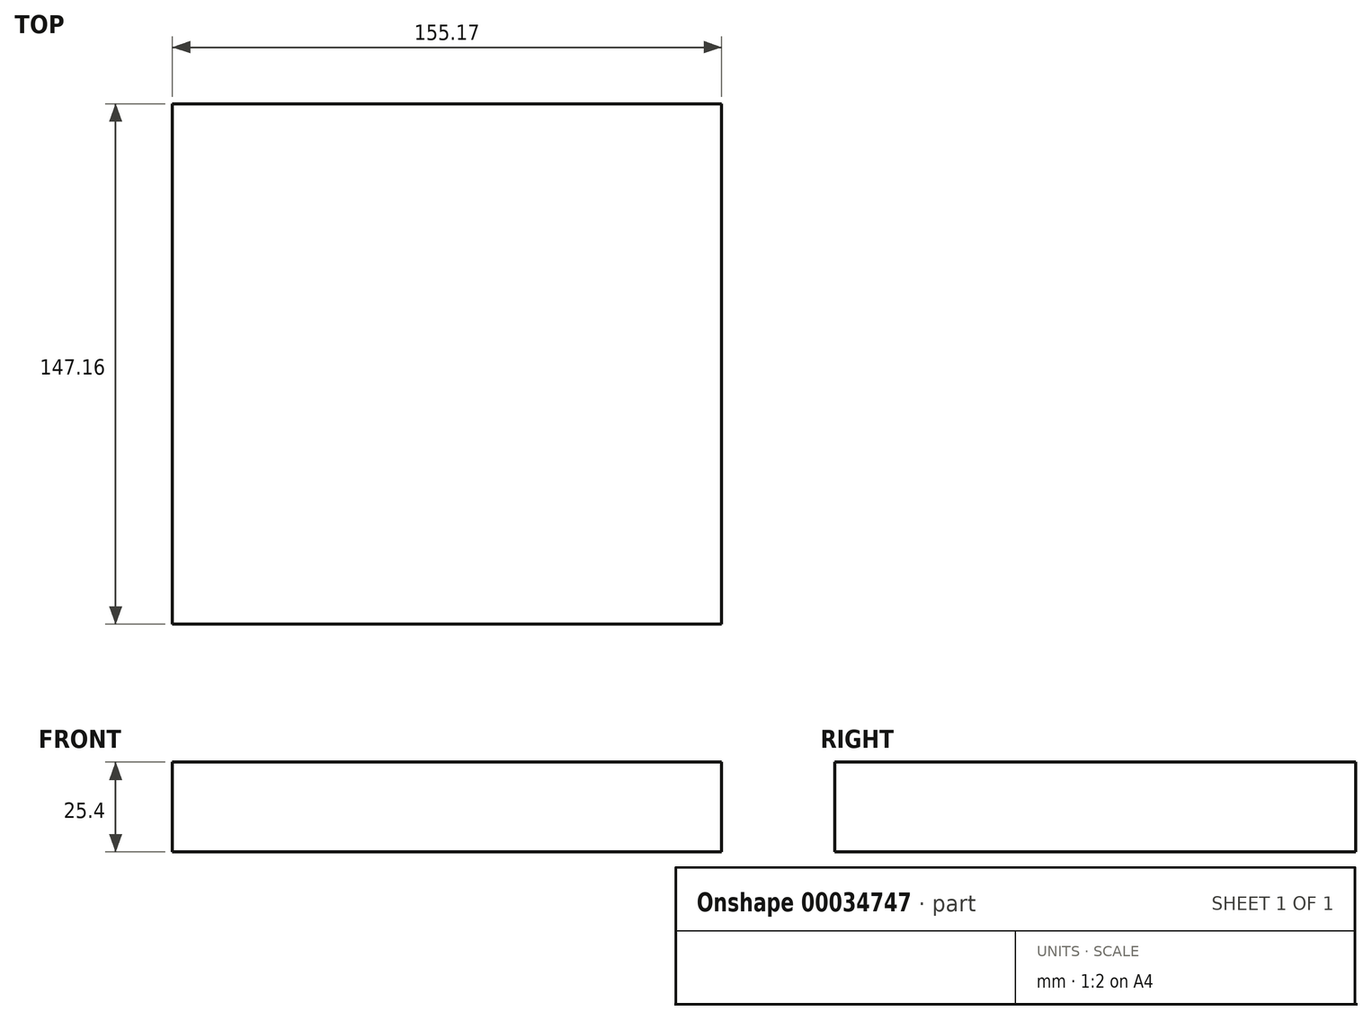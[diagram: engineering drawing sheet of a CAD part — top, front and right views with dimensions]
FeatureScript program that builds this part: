
annotation { "Feature Type Name" : "Feature", "Feature Type Description" : "" }
export const myFeature = defineFeature(function(context is Context, id is Id, definition is map)
    precondition{}
    {
        {
            var Q0;
            Q0=qCreatedBy(makeId("Top.planeOp"),FACE);
            var sketch = newSketch(context, id + "F0", { "sketchPlane" : qUnion([Q0])});
            skLineSegment(sketch, "E0.bottom", {"start": v(-76.18, 71.48) * mm, "end": v(79, 71.48) * mm});
            skLineSegment(sketch, "E0.top", {"start": v(-76.18, -75.68) * mm, "end": v(79, -75.68) * mm});
            skLineSegment(sketch, "E0.left", {"start": v(-76.18, 71.48) * mm, "end": v(-76.18, -75.68) * mm});
            skLineSegment(sketch, "E0.right", {"start": v(79, 71.48) * mm, "end": v(79, -75.68) * mm});
            skLineSegment(sketch, "E1.bottom", {"start": v(210.44, -47.96) * mm, "end": v(212.67, -47.96) * mm});
            skLineSegment(sketch, "E1.top", {"start": v(210.44, 119.08) * mm, "end": v(212.67, 119.08) * mm});
            skLineSegment(sketch, "E1.left", {"start": v(210.44, -47.96) * mm, "end": v(210.44, 119.08) * mm});
            skLineSegment(sketch, "E1.right", {"start": v(212.67, -47.96) * mm, "end": v(212.67, 119.08) * mm});
            skSolve(sketch);
        }
        {
            var Q0;
            Q0=makeQuery(id+"F0.imprint","IMPRINT",FACE,{"disambiguationData":[TD([[makeQuery(id+"F0.imprint","IMPRINT",EDGE,{"derivedFrom":sQuery(id+"F0.wireOp",EDGE,"E0.bottom")}),-1.0]])]});
            extrude(context, id + "F1", {"entities" : qUnion([Q0]), "depth" : 25.4 * mm});
        }
    });
